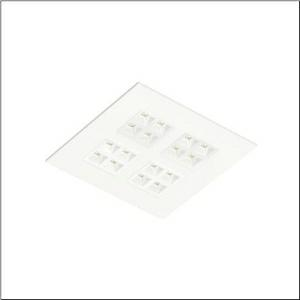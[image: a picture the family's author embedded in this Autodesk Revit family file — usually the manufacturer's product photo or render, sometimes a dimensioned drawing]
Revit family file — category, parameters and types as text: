
# Revit family: silica_r__31_square_51my6nmu34wa_2aeb
name_source: partatom
category: Lighting Fixtures
units: mm (PartAtom-declared; Revit-internal decimal feet)

## family parameters
Cut with Voids When Loaded = No
Host = Face
Light Source = No
Part Type = Normal
Room Calculation Point = No
Round Connector Dimension = Use Diameter
Shared = No

## types (1)
- --- (1 x LED, 6600 lm, 39 W, 3000K)
    Apparent Load = 39 VA
    CIE Flux Codes = 81 99 100 100 100
    Color Rendering = 80
    Color Temperature = 3000K
    Default Elevation = 1800 mm
    Description = Silica® 31 Square, office luminaire, primary light control with lens, of PMMA, primary anti-glare with reflector, of PC, white, light emission: direct distribution, primary light characteristic: symmetric, installation type: lay-in mounting, LED, rated luminous flux: 4.580lm, luminous efficacy: 176lm/W, light colour: 830, colour temperature: 3000K, control gear: ON/OFF Multilumen, with terminal, 3-pole, mains connection: 220..240V, AC, 50/60Hz, rated input power: 26W, luminaire housing, of sheet steel, coated, traffic white (RAL 9016), module: M625, length: 620mm, width: 620mm, height: 43mm, protection rating (complete): IP20, insulation class (complete): insulation class II (safety insulation), certification: CE, impact resistance: IK03, permissible operating ambient temperature: -20..+35°C, standard: EN 50419, packaging unit: 1 piece
    Height = 0 mm  [stored 0 ft]
    Lamp = 1 x LED
    Lamp Light Flux = 6600 lm
    Lamp Power = 39 W
    Lamp count = 1
    Length = 620 mm
    Luminous efficacy = 169 lm/W
    Manufacturer = Siteco
    ModVariant = No
    Model = 51MY6NMU34WA
    Mounting Place = Ceiling
    Mounting Type = Recessed
    Number of Poles = 1
    OnlyDefault = Yes
    Power Factor = 1
    Product Name = Silica® 31 Square
    Product group = office luminaire | ceiling recessed
    ProductGroupID = 401
    Protection Class = Protection class II
    Protection Degree = IP 20
    RLX_Detail_Level = 1
    RLX_Emergency_Light_Flux = 0 lm
    RLX_Emergency_Type = 0
    RLX_Emergency_Type_DB = No
    RlxData = <blob elided: 28505 chars, md5=f4df0b54>
    Socket = socket
    Standby Power = 0 W
    System Light Flux = 6600 lm
    System Power = 39 W
    Type Comments = factory setting: luminous flux: 100 % | (ON | ON | ON | ON) | 1100 mA
    Type Image = l_1313651.jpg
    URL = http://relux.com
    VarID = @adj_036066
    Voltage = 0 V
    Weight = 0.00 kg
    Width = 620 mm

note: [stored X ft] marks values corroborated as IEEE doubles in the binary element streams (Revit-internal decimal feet)

## geometry (parser evidence)
native form markers: Blend x4, Sweep x9
no freeform markers — native parametric forms only
